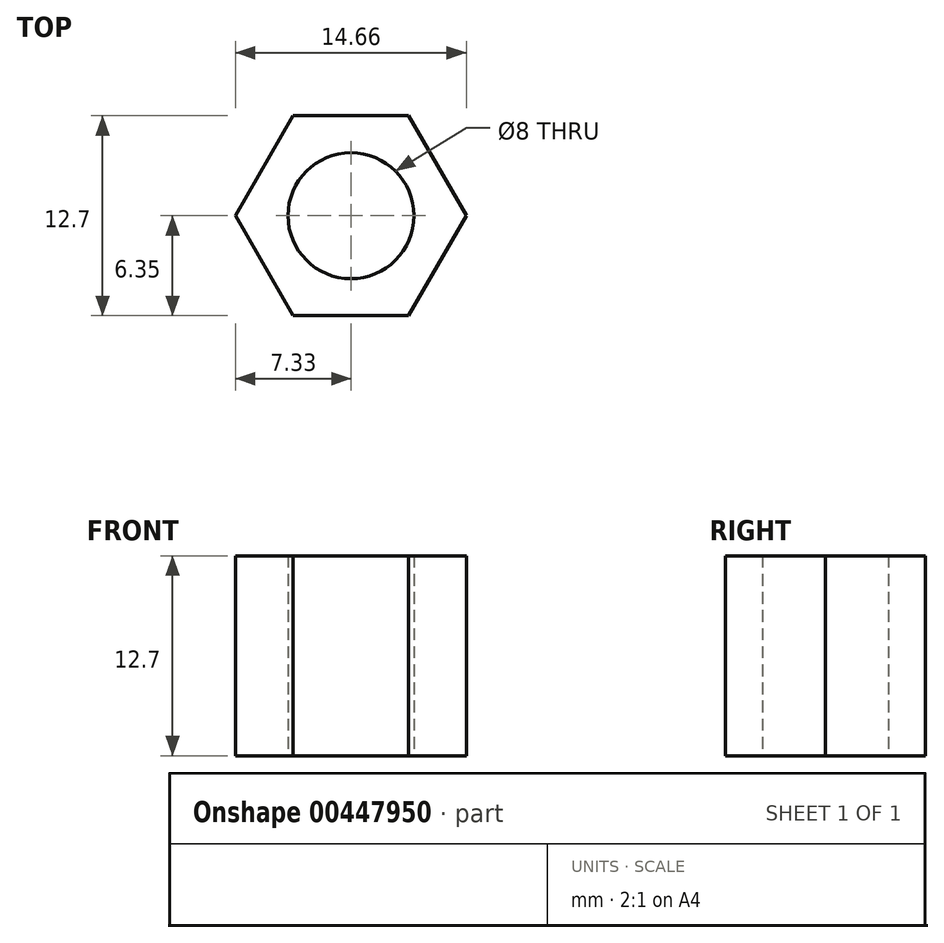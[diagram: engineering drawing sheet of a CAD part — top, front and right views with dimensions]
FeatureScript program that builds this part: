
annotation { "Feature Type Name" : "Feature", "Feature Type Description" : "" }
export const myFeature = defineFeature(function(context is Context, id is Id, definition is map)
    precondition{}
    {
        {
            var Q0;
            Q0=qCreatedBy(makeId("Top.planeOp"),FACE);
            var sketch = newSketch(context, id + "F0", { "sketchPlane" : qUnion([Q0])});
            skCircle(sketch, "E0.cCircle", {"center": v(0, 0) * mm, "radius": 6.35 * mm, "construction": true});
            skLineSegment(sketch, "E0.0", {"start": v(-3.67, 6.35) * mm, "end": v(3.67, 6.35) * mm});
            skLineSegment(sketch, "E0.1", {"start": v(3.67, 6.35) * mm, "end": v(7.33, 0) * mm});
            skLineSegment(sketch, "E0.2", {"start": v(7.33, 0) * mm, "end": v(3.67, -6.35) * mm});
            skLineSegment(sketch, "E0.3", {"start": v(3.67, -6.35) * mm, "end": v(-3.67, -6.35) * mm});
            skLineSegment(sketch, "E0.4", {"start": v(-3.67, -6.35) * mm, "end": v(-7.33, 0) * mm});
            skLineSegment(sketch, "E0.5", {"start": v(-7.33, 0) * mm, "end": v(-3.67, 6.35) * mm});
            skPoint(sketch, "E0.0.midPoint", {"position": v(0, 6.35) * mm});
            skCircle(sketch, "E1", {"center": v(0, 0) * mm, "radius": 4 * mm});
            skSolve(sketch);
        }
        {
            var Q0;
            Q0=makeQuery(id+"F0.imprint","IMPRINT",FACE,{"disambiguationData":[TD([[makeQuery(id+"F0.imprint","IMPRINT",EDGE,{"derivedFrom":sQuery(id+"F0.wireOp",EDGE,"E0.0")}),-1.0]])]});
            extrude(context, id + "F1", {"entities" : qUnion([Q0]), "depth" : 12.7 * mm});
        }
    });
